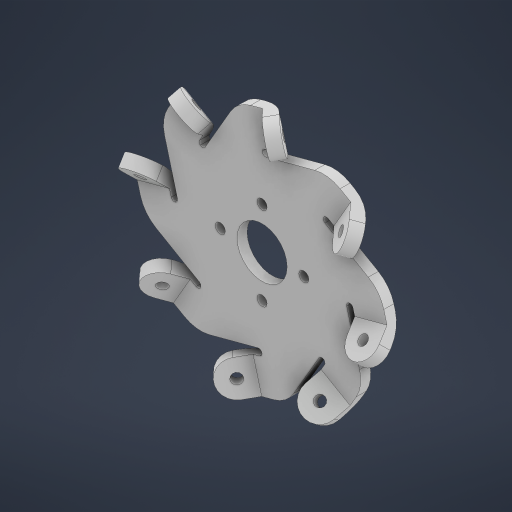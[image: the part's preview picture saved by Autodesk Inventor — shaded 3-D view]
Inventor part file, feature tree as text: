
AUTODESK INVENTOR PART (.ipt)
format: ipt  version: 2023 (Build 270158000, 158)  size: 394,752 bytes
history: native  units: mm
features: extrude x3, fillet x3, sketch x3, pattern_circular x2, plane x1
ambient origin geometry x8: Origin, YZ Plane, XZ Plane, XY Plane, X Axis, Y Axis, Z Axis, Center Point
bodies: Solid1 (feature_tree)
feature tree (12):
  extrude  "Extrusion1"  Depth=50.0mm
  plane  "Work Plane1"
  extrude  "Extrusion2"  Depth=3.0mm
  fillet  "Fillet1"  Radius=3.0mm
  extrude  "Extrusion3"  Depth=1.0mm
  pattern_circular  "Circular Pattern1"  [2 undecoded]
  fillet  "Fillet2"  [1 undecoded]
  fillet  "Fillet3"  Radius=10.0mm
  pattern_circular  "Circular Pattern2"  [2 undecoded]
  sketch  "Sketch1"  dims[d0=15.0mm d1=50.0mm]
  sketch  "Sketch2"  dims[d3=3.0mm d4=3.0mm d5=3.0mm]
  sketch  "Sketch3"  dims[d6=3.0mm d8=2.0mm d13=5.0mm d14=30.0deg d15=10.0mm d16=10.0mm d17=80.0mm d19=360.0deg d21=3.0mm d22=0.0mm d23=135.0deg d24=10.0mm d25=0.0mm d26=5.0mm d27=3.0mm d28=10.0mm d29=0.0mm d30=80.0mm d31=360.0deg d33=10.0mm d34=1.0mm d35=80.0mm d36=360.0deg]
note: 5 required parameter values undecoded (feature->parameter linkage not recoverable at this tier; creation-order binding heuristic only, values carry confidence <= 0.55)
